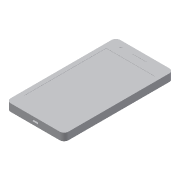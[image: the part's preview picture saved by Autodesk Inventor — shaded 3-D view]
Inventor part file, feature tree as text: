
AUTODESK INVENTOR PART (.ipt)
format: ipt  version: 2013 (Build 170138000, 138)  size: 133,632 bytes
history: native  units: mm
features: extrude x4, fillet x4, sketch x4, projected_geometry x1
ambient origin geometry x8: Origin, YZ Plane, XZ Plane, XY Plane, X Axis, Y Axis, Z Axis, Center Point
bodies: Volumenkörper1 (feature_tree)
feature tree (13):
  extrude  "Extrusion1"  Depth=125.3mm
  fillet  "Rundung1"  Radius=8.5mm
  fillet  "Rundung2"  Radius=5.0mm
  fillet  "Rundung3"  Radius=5.0mm
  fillet  "Rundung4"  Radius=5.0mm
  sketch  "Skizze2"  dims[d7=5.0mm d8=56.0mm]
  extrude  "Extrusion2"  Depth=56.0mm
  extrude  "Extrusion3"  Depth=5.05mm
  extrude  "Extrusion4"  Depth=6.7mm
  sketch  "Skizze1"  dims[d0=66.1mm d1=125.3mm d2=8.5mm d3=0.0mm d4=5.0mm d5=5.0mm d6=5.0mm]
  sketch  "Skizze3"  dims[d9=93.0mm d10=5.05mm]
  sketch  "Skizze5"  dims[d11=16.15mm d12=6.7mm d13=12.0mm d14=3.0mm d19=1.4mm d22=5.6mm d23=15.7mm d27=14.3mm d28=25.9mm d29=0.2mm d30=0.0mm d31=0.2mm d32=0.0mm d33=6.85mm d34=1.8mm d35=24.575mm d36=3.35mm d37=2.0mm d38=0.0mm]
  projected_geometry  "Projizierte Kontur2"
